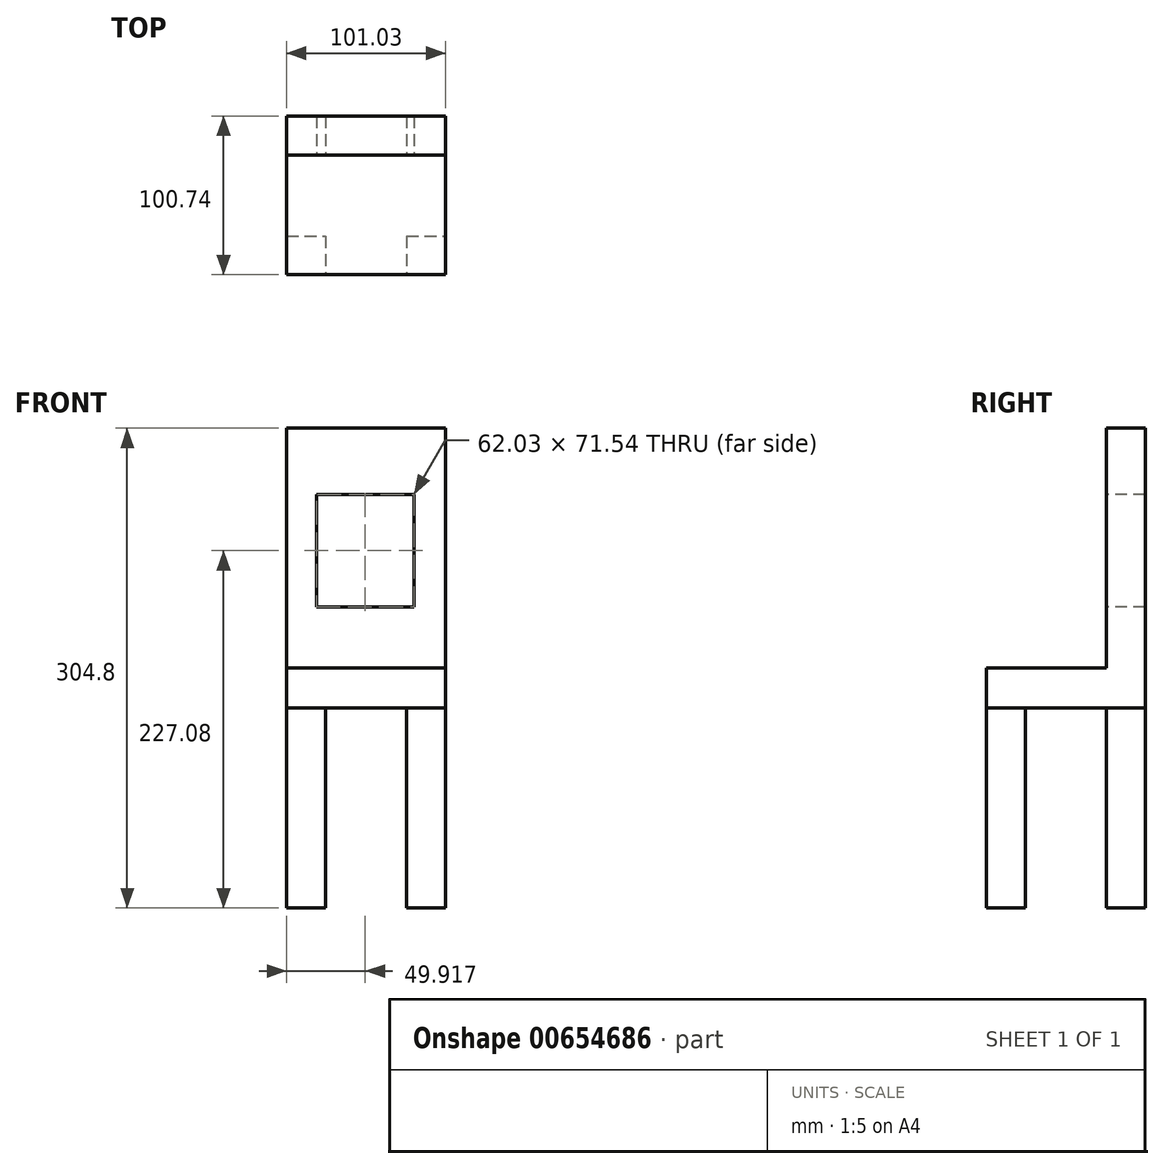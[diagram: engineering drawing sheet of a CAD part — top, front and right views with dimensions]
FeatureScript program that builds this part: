
annotation { "Feature Type Name" : "Feature", "Feature Type Description" : "" }
export const myFeature = defineFeature(function(context is Context, id is Id, definition is map)
    precondition{}
    {
        {
            var Q0;
            Q0=qCreatedBy(makeId("Top.planeOp"),FACE);
            var sketch = newSketch(context, id + "F0", { "sketchPlane" : qUnion([Q0])});
            skLineSegment(sketch, "E0.bottom", {"start": v(-44.82, 45.99) * mm, "end": v(-20, 45.99) * mm});
            skLineSegment(sketch, "E0.top", {"start": v(-44.82, 21.46) * mm, "end": v(-20, 21.46) * mm});
            skLineSegment(sketch, "E0.left", {"start": v(-44.82, 45.99) * mm, "end": v(-44.82, 21.46) * mm});
            skLineSegment(sketch, "E0.right", {"start": v(-20, 45.99) * mm, "end": v(-20, 21.46) * mm});
            skSolve(sketch);
        }
        {
            var Q0;
            Q0 = qSketchRegion(id + "F0", true);
            extrude(context, id + "F1", {"entities" : qUnion([Q0]), "depth" : 127 * mm, "offsetDistance" : 25.4 * mm});
        }
        {
            var Q0;
            Q0=makeQuery(id+"F1.opExtrude","SWEPT_BODY",BODY,{"disambiguationData":[OSD([sQuery(id+"F0.wireOp",EDGE,"E0.bottom"),sQuery(id+"F0.wireOp",EDGE,"E0.top"),sQuery(id+"F0.wireOp",EDGE,"E0.left"),sQuery(id+"F0.wireOp",EDGE,"E0.right")])]});
            transform(context, id + "F2", {"entities" : qUnion([Q0]), "transformType" : TransformType.TRANSLATION_3D, "dx" : 76.2 * mm, "dy" : 0 * mm, "dz" : 0 * mm, "makeCopy" : true});
        }
        {
            var Q0;
            Q0=makeQuery(id+"F2.opPattern","COPY",BODY,{"derivedFrom":makeQuery(id+"F1.opExtrude","SWEPT_BODY",BODY,{"disambiguationData":[OSD([sQuery(id+"F0.wireOp",EDGE,"E0.bottom"),sQuery(id+"F0.wireOp",EDGE,"E0.top"),sQuery(id+"F0.wireOp",EDGE,"E0.left"),sQuery(id+"F0.wireOp",EDGE,"E0.right")])]}),"instanceName":"1"});
            transform(context, id + "F3", {"entities" : qUnion([Q0]), "transformType" : TransformType.TRANSLATION_3D, "dx" : 0 * mm, "dy" : -76.2 * mm, "dz" : 0 * mm, "makeCopy" : true});
        }
        {
            var Q0;
            Q0=makeQuery(id+"F3.opPattern","COPY",BODY,{"derivedFrom":makeQuery(id+"F2.opPattern","COPY",BODY,{"derivedFrom":makeQuery(id+"F1.opExtrude","SWEPT_BODY",BODY,{"disambiguationData":[OSD([sQuery(id+"F0.wireOp",EDGE,"E0.bottom"),sQuery(id+"F0.wireOp",EDGE,"E0.top"),sQuery(id+"F0.wireOp",EDGE,"E0.left"),sQuery(id+"F0.wireOp",EDGE,"E0.right")])]}),"instanceName":"1"}),"instanceName":"1"});
            transform(context, id + "F4", {"entities" : qUnion([Q0]), "transformType" : TransformType.TRANSLATION_3D, "dx" : -76.2 * mm, "dy" : 0 * mm, "dz" : 0 * mm, "makeCopy" : true});
        }
        {
            var Q0;
            Q0=makeQuery(id+"F1.opExtrude","CAP_FACE",FACE,{"disambiguationData":[OSD([sQuery(id+"F0.wireOp",EDGE,"E0.bottom"),sQuery(id+"F0.wireOp",EDGE,"E0.top"),sQuery(id+"F0.wireOp",EDGE,"E0.left"),sQuery(id+"F0.wireOp",EDGE,"E0.right")])],"isStart":false});
            var sketch = newSketch(context, id + "F5", { "sketchPlane" : qUnion([Q0])});
            skLineSegment(sketch, "E1.bottom", {"start": v(-44.82, 45.99) * mm, "end": v(56.21, 45.99) * mm});
            skLineSegment(sketch, "E1.top", {"start": v(-44.82, -54.75) * mm, "end": v(56.21, -54.75) * mm});
            skLineSegment(sketch, "E1.left", {"start": v(-44.82, 45.99) * mm, "end": v(-44.82, -54.75) * mm});
            skLineSegment(sketch, "E1.right", {"start": v(56.21, 45.99) * mm, "end": v(56.21, -54.75) * mm});
            skSolve(sketch);
        }
        {
            var Q0;
            Q0 = qSketchRegion(id + "F5", true);
            extrude(context, id + "F6", {"entities" : qUnion([Q0]), "depth" : 25.4 * mm, "offsetDistance" : 25.4 * mm});
        }
        {
            var Q0;
            Q0=makeQuery(id+"F6.opExtrude","CAP_FACE",FACE,{"disambiguationData":[OSD([sQuery(id+"F5.wireOp",EDGE,"E1.bottom"),sQuery(id+"F5.wireOp",EDGE,"E1.top"),sQuery(id+"F5.wireOp",EDGE,"E1.left"),sQuery(id+"F5.wireOp",EDGE,"E1.right")])],"isStart":false});
            var sketch = newSketch(context, id + "F7", { "sketchPlane" : qUnion([Q0])});
            skLineSegment(sketch, "E2.bottom", {"start": v(-44.82, 45.99) * mm, "end": v(56.21, 45.99) * mm});
            skLineSegment(sketch, "E2.top", {"start": v(-44.82, 21.17) * mm, "end": v(56.21, 21.17) * mm});
            skLineSegment(sketch, "E2.left", {"start": v(-44.82, 45.99) * mm, "end": v(-44.82, 21.17) * mm});
            skLineSegment(sketch, "E2.right", {"start": v(56.21, 45.99) * mm, "end": v(56.21, 21.17) * mm});
            skSolve(sketch);
        }
        {
            var Q0;
            Q0 = qSketchRegion(id + "F7", true);
            extrude(context, id + "F8", {"entities" : qUnion([Q0]), "operationType" : NewBodyOperationType.ADD, "depth" : 152.4 * mm, "offsetDistance" : 25.4 * mm});
        }
        {
            var Q0;
            Q0=makeQuery(id+"F8.opExtrude","SWEPT_FACE",FACE,{"disambiguationData":[OSD([sQuery(id+"F7.wireOp",EDGE,"E2.top")])]});
            var sketch = newSketch(context, id + "F9", { "sketchPlane" : qUnion([Q0])});
            skLineSegment(sketch, "E3.bottom", {"start": v(-25.92, 262.85) * mm, "end": v(36.1, 262.85) * mm});
            skLineSegment(sketch, "E3.top", {"start": v(-25.92, 191.3) * mm, "end": v(36.1, 191.3) * mm});
            skLineSegment(sketch, "E3.left", {"start": v(-25.92, 262.85) * mm, "end": v(-25.92, 191.3) * mm});
            skLineSegment(sketch, "E3.right", {"start": v(36.1, 262.85) * mm, "end": v(36.1, 191.3) * mm});
            skSolve(sketch);
        }
        {
            var Q0;
            Q0=makeQuery(id+"F9.imprint","IMPRINT",FACE,{"disambiguationData":[TD([[makeQuery(id+"F9.imprint","IMPRINT",EDGE,{"derivedFrom":sQuery(id+"F9.wireOp",EDGE,"E3.bottom")}),-1.0]])]});
            extrude(context, id + "F10", {"entities" : qUnion([Q0]), "operationType" : NewBodyOperationType.REMOVE, "oppositeDirection" : true, "depth" : 101.6 * mm, "offsetDistance" : 25.4 * mm});
        }
    });
